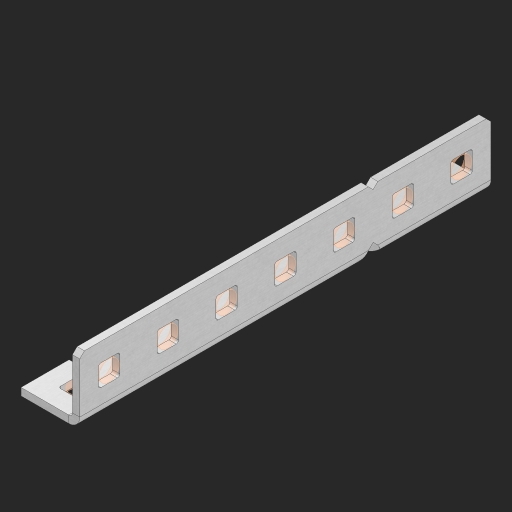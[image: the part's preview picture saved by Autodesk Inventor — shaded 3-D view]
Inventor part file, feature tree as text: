
AUTODESK INVENTOR PART (.ipt)
format: ipt  version: 2023 (Build 270158000, 158)  size: 573,952 bytes
history: native  units: in
note: dims shown in document units (in); Inventor stores cm internally (conversion verified against a paired STEP export)
features: other x169, extrude x19, sheet_metal_op x11, sketch x10, pattern_linear x2, mirror x1, chamfer x1
ambient origin geometry x8: Origin, YZ Plane, XZ Plane, XY Plane, X Axis, Y Axis, Z Axis, Center Point
bodies: Solid1 (feature_tree), Body (feature_tree)
feature tree (213):
  other  "Alu Half C 1x2x1x7"
  other  "Table"
  other  "Alu C 1x2x1x35"
  other  "Alu C 1x2x1x34"
  other  "Alu C 1x2x1x33"
  other  "Alu C 1x2x1x32"
  other  "Alu C 1x2x1x31"
  other  "Alu C 1x2x1x30"
  other  "Alu C 1x2x1x29"
  other  "Alu C 1x2x1x28"
  other  "Alu C 1x2x1x27"
  other  "Alu C 1x2x1x26"
  other  "Alu C 1x2x1x25"
  other  "Alu C 1x2x1x24"
  other  "Alu C 1x2x1x23"
  other  "Alu C 1x2x1x22"
  other  "Alu C 1x2x1x21"
  other  "Alu C 1x2x1x20"
  other  "Alu C 1x2x1x19"
  other  "Alu C 1x2x1x18"
  other  "Alu C 1x2x1x17"
  other  "Alu C 1x2x1x16"
  other  "Alu C 1x2x1x15"
  other  "Alu C 1x2x1x14"
  other  "Alu C 1x2x1x13"
  other  "Alu C 1x2x1x12"
  other  "Alu C 1x2x1x11"
  other  "Alu C 1x2x1x10"
  other  "Alu C 1x2x1x9"
  other  "Alu C 1x2x1x8"
  other  "Alu C 1x2x1x7"
  other  "Alu C 1x2x1x6"
  other  "Alu C 1x2x1x5"
  other  "Alu C 1x2x1x4"
  other  "Alu C 1x2x1x3"
  other  "Alu C 1x2x1x2"
  other  "Alu C 1x2x1x1"
  other  "Steel C 1x2x1x35"
  other  "Steel C 1x2x1x34"
  other  "Steel C 1x2x1x33"
  other  "Steel C 1x2x1x32"
  other  "Steel C 1x2x1x31"
  other  "Steel C 1x2x1x30"
  other  "Steel C 1x2x1x29"
  other  "Steel C 1x2x1x28"
  other  "Steel C 1x2x1x27"
  other  "Steel C 1x2x1x26"
  other  "Steel C 1x2x1x25"
  other  "Steel C 1x2x1x24"
  other  "Steel C 1x2x1x23"
  other  "Steel C 1x2x1x22"
  other  "Steel C 1x2x1x21"
  other  "Steel C 1x2x1x20"
  other  "Steel C 1x2x1x19"
  other  "Steel C 1x2x1x18"
  other  "Steel C 1x2x1x17"
  other  "Steel C 1x2x1x16"
  other  "Steel C 1x2x1x15"
  other  "Steel C 1x2x1x14"
  other  "Steel C 1x2x1x13"
  other  "Steel C 1x2x1x12"
  other  "Steel C 1x2x1x11"
  other  "Steel C 1x2x1x10"
  other  "Steel C 1x2x1x9"
  other  "Steel C 1x2x1x8"
  other  "Steel C 1x2x1x7"
  other  "Steel C 1x2x1x6"
  other  "Steel C 1x2x1x5"
  other  "Steel C 1x2x1x4"
  other  "Steel C 1x2x1x3"
  other  "Steel C 1x2x1x2"
  other  "Steel C 1x2x1x1"
  other  "Alu Half C 1x2x1x35"
  other  "Alu Half C 1x2x1x34"
  other  "Alu Half C 1x2x1x33"
  other  "Alu Half C 1x2x1x32"
  other  "Alu Half C 1x2x1x31"
  other  "Alu Half C 1x2x1x30"
  other  "Alu Half C 1x2x1x29"
  other  "Alu Half C 1x2x1x28"
  other  "Alu Half C 1x2x1x27"
  other  "Alu Half C 1x2x1x26"
  other  "Alu Half C 1x2x1x25"
  other  "Alu Half C 1x2x1x24"
  other  "Alu Half C 1x2x1x23"
  other  "Alu Half C 1x2x1x22"
  other  "Alu Half C 1x2x1x21"
  other  "Alu Half C 1x2x1x20"
  other  "Alu Half C 1x2x1x19"
  other  "Alu Half C 1x2x1x18"
  other  "Alu Half C 1x2x1x17"
  other  "Alu Half C 1x2x1x16"
  other  "Alu Half C 1x2x1x15"
  other  "Alu Half C 1x2x1x14"
  other  "Alu Half C 1x2x1x13"
  other  "Alu Half C 1x2x1x12"
  other  "Alu Half C 1x2x1x11"
  other  "Alu Half C 1x2x1x10"
  other  "Alu Half C 1x2x1x9"
  other  "Alu Half C 1x2x1x8"
  other  "Alu Half C 1x2x1x6"
  other  "Alu Half C 1x2x1x5"
  other  "Alu Half C 1x2x1x4"
  other  "Alu Half C 1x2x1x3"
  other  "Alu Half C 1x2x1x2"
  other  "Alu Half C 1x2x1x1"
  other  "Steel Half C 1x2x1x35"
  other  "Steel Half C 1x2x1x34"
  other  "Steel Half C 1x2x1x33"
  other  "Steel Half C 1x2x1x32"
  other  "Steel Half C 1x2x1x31"
  other  "Steel Half C 1x2x1x30"
  other  "Steel Half C 1x2x1x29"
  other  "Steel Half C 1x2x1x28"
  other  "Steel Half C 1x2x1x27"
  other  "Steel Half C 1x2x1x26"
  other  "Steel Half C 1x2x1x25"
  other  "Steel Half C 1x2x1x24"
  other  "Steel Half C 1x2x1x23"
  other  "Steel Half C 1x2x1x22"
  other  "Steel Half C 1x2x1x21"
  other  "Steel Half C 1x2x1x20"
  other  "Steel Half C 1x2x1x19"
  other  "Steel Half C 1x2x1x18"
  other  "Steel Half C 1x2x1x17"
  other  "Steel Half C 1x2x1x16"
  other  "Steel Half C 1x2x1x15"
  other  "Steel Half C 1x2x1x14"
  other  "Steel Half C 1x2x1x13"
  other  "Steel Half C 1x2x1x12"
  other  "Steel Half C 1x2x1x11"
  other  "Steel Half C 1x2x1x10"
  other  "Steel Half C 1x2x1x9"
  other  "Steel Half C 1x2x1x8"
  other  "Steel Half C 1x2x1x7"
  other  "Steel Half C 1x2x1x6"
  other  "Steel Half C 1x2x1x5"
  other  "Steel Half C 1x2x1x4"
  other  "Steel Half C 1x2x1x3"
  other  "Steel Half C 1x2x1x2"
  other  "Steel Half C 1x2x1x1"
  sheet_metal_op  "Flanges"
  other  "Flange Pattern Plane"
  other  "Flange Pattern Sketch"
  sheet_metal_op  "Flange Pattern"
  sheet_metal_op  "Body Pattern"
  pattern_linear  "Center Pattern"  Spacing1=0.0625in  [1 undecoded]
  other  "Arc Length"
  mirror  "Notch Mirror"
  pattern_linear  "Notch Pattern"  Spacing1=0.182in  [1 undecoded]
  chamfer  "End Chamfer"
  extrude  "Half Cut"  Depth=0.02in
  sketch  "Sketch1"  dims[d0=1.0in]
  other  "Plate1"
  sketch  "Sketch2"  dims[d1=3.5in]
  other  "Plate2"
  sheet_metal_op  "Bend1"
  sheet_metal_op  "Corner1"
  sketch  "Sketch3"  dims[d2=0.0625in]
  sketch  "Sketch7"  dims[d3=0.0625in]
  other  "Srf1"
  other  "Srf2"
  sketch  "Sketch8"  dims[d4=0.0312in]
  sketch  "Sketch9"  dims[d5=0.125in]
  other  "Srf91"
  sheet_metal_op  "Body Pattern Sketch"
  other  "Srf92"
  sketch  "Sketch13"  dims[d6=0.0625in]
  sketch  "Sketch14"  dims[d7=0.5in d8=90.0deg d9=0.0312in]
  sketch  "Sketch15"  dims[d10=0.25in]
  sketch  "Sketch16"  dims[d11=0.0625in d12=0.0625in d16=0.182in d17=0.02in d18=0.0625in d19=0.0in d20=0.25in d21=0.25in d38=2.7559in d40=0.5in d41=0.3937in d43=1.0in d46=0.172in d47=1.0in d48=0.0in d49=0.182in d50=0.02in d51=0.25in d52=0.25in d53=0.0625in d54=0.0in d55=0.172in d56=1.0in d57=0.0in d58=0.25in d60=2.7559in d62=0.5in d63=0.3937in d65=0.5in d85=0.1473in d86=0.1782in d88=0.04in d89=0.0625in d90=0.0in d91=0.04in d92=0.0491in d95=2.5in d96=0.04in d97=0.25in d98=45.0deg d99=0.25in d100=0.5in d101=0.0in d102=2.497in d106=0.182in d107=0.02in d108=0.5in d109=0.5in d110=0.0625in d111=0.0in d112=0.172in d113=0.5in d114=0.0in d117=0.5in d118=0.5in d119=0.5in]
  other  "Srf786"
  other  "Srf823"
  other  "Srf824"
  other  "Srf825"
  other  "Srf826"
  other  "Srf827"
  other  "Srf856"
  other  "Srf857"
  other  "Srf858"
  other  "Srf859"
  other  "Srf860"
  other  "Srf889"
  other  "Srf890"
  other  "Srf891"
  other  "Srf892"
  other  "Srf893"
  other  "Srf894"
  sheet_metal_op  "Flange Stamp"
  sheet_metal_op  "Flange Circle"
  sheet_metal_op  "Body Stamp"
  sheet_metal_op  "Body Circle"
  other  "Center Stamp"
  other  "Center Circle"
  sheet_metal_op  "Notch"
  extrude  "ExtrusionSrf2"  Depth=0.0625in
  extrude  "ExtrusionSrf92"  TaperAngle=0.0deg  [1 undecoded]
  extrude  "ExtrusionSrf823"  Depth=0.5in
  extrude  "ExtrusionSrf824"  Depth=0.5in
  extrude  "ExtrusionSrf825"  Depth=0.5in
  extrude  "ExtrusionSrf826"  Depth=0.5in
  extrude  "ExtrusionSrf827"  Depth=1.0in TaperAngle=0.0deg
  extrude  "ExtrusionSrf856"  Depth=0.182in
  extrude  "ExtrusionSrf857"  Depth=0.02in
  extrude  "ExtrusionSrf858"  Depth=0.5in
  extrude  "ExtrusionSrf859"  Depth=0.5in
  extrude  "ExtrusionSrf860"  Depth=0.0625in
  extrude  "ExtrusionSrf889"  TaperAngle=0.0deg  [1 undecoded]
  extrude  "ExtrusionSrf890"  Depth=0.5in
  extrude  "ExtrusionSrf891"  Depth=1.0in TaperAngle=0.0deg
  extrude  "ExtrusionSrf892"  Depth=0.5in
  extrude  "ExtrusionSrf893"  Depth=0.5in
  extrude  "ExtrusionSrf894"  Depth=0.5in
note: 4 required parameter values undecoded (feature->parameter linkage not recoverable at this tier; creation-order binding heuristic only, values carry confidence <= 0.55)
